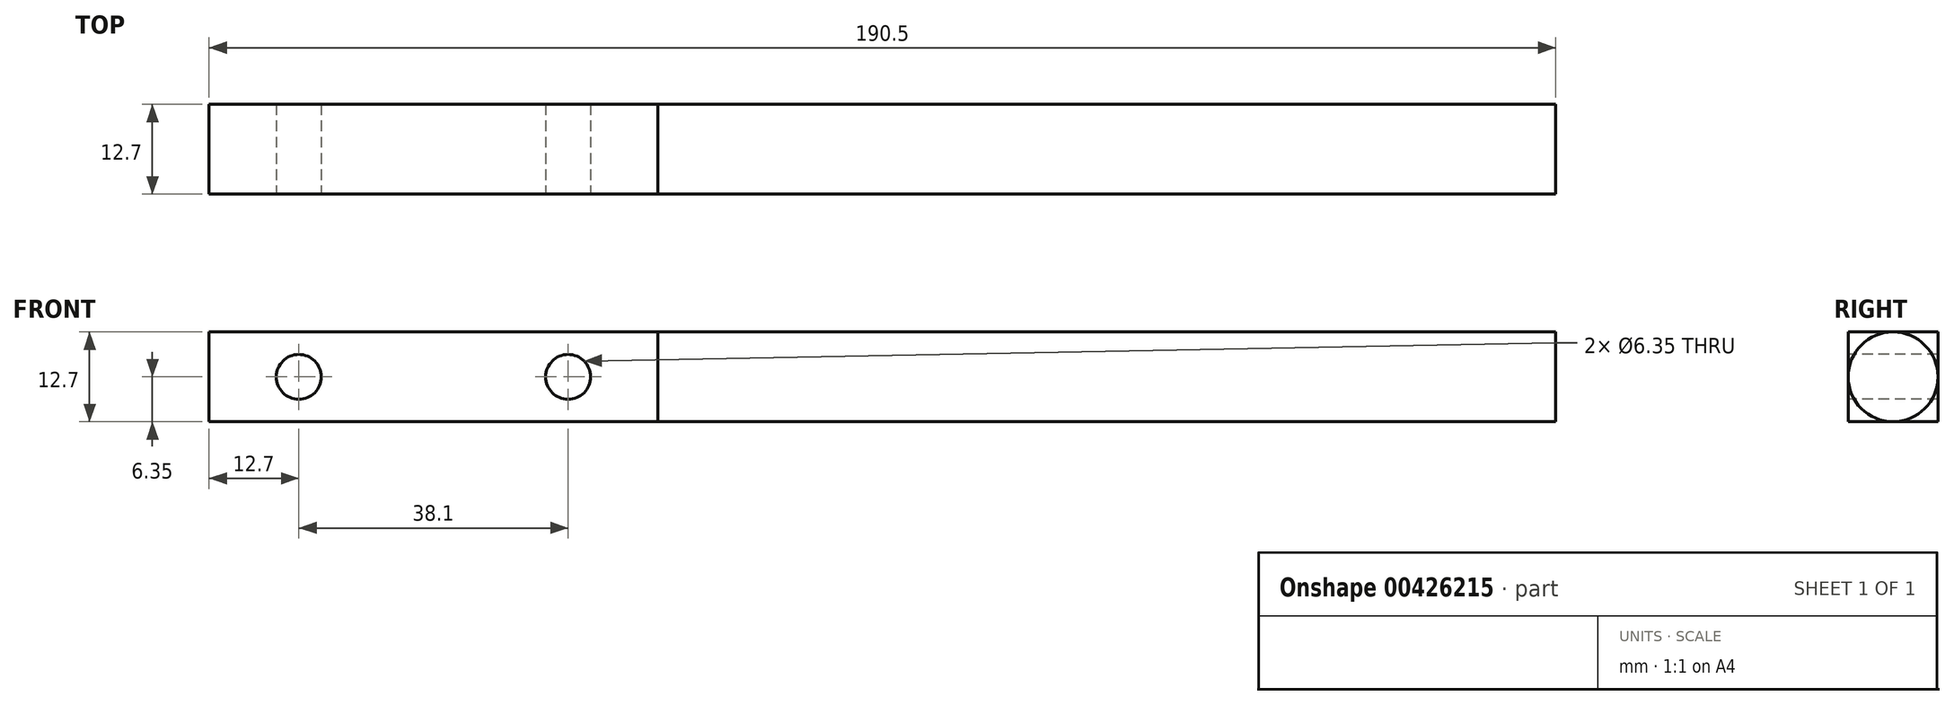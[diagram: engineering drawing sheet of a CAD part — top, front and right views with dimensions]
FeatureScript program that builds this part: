
annotation { "Feature Type Name" : "Feature", "Feature Type Description" : "" }
export const myFeature = defineFeature(function(context is Context, id is Id, definition is map)
    precondition{}
    {
        {
            var Q0;
            Q0=qCreatedBy(makeId("Right.planeOp"),FACE);
            var sketch = newSketch(context, id + "F0", { "sketchPlane" : qUnion([Q0])});
            skLineSegment(sketch, "E0.bottom", {"start": v(0, 0) * mm, "end": v(12.7, 0) * mm});
            skLineSegment(sketch, "E0.top", {"start": v(0, 12.7) * mm, "end": v(12.7, 12.7) * mm});
            skLineSegment(sketch, "E0.left", {"start": v(0, 0) * mm, "end": v(0, 12.7) * mm});
            skLineSegment(sketch, "E0.right", {"start": v(12.7, 0) * mm, "end": v(12.7, 12.7) * mm});
            skSolve(sketch);
        }
        {
            var Q0;
            Q0 = qSketchRegion(id + "F0", true);
            extrude(context, id + "F1", {"entities" : qUnion([Q0]), "depth" : 63.5 * mm});
        }
        {
            var Q0;
            Q0=makeQuery(id+"F1.opExtrude","CAP_FACE",FACE,{"disambiguationData":[OSD([sQuery(id+"F0.wireOp",EDGE,"E0.bottom"),sQuery(id+"F0.wireOp",EDGE,"E0.top"),sQuery(id+"F0.wireOp",EDGE,"E0.left"),sQuery(id+"F0.wireOp",EDGE,"E0.right")])],"isStart":false});
            var sketch = newSketch(context, id + "F2", { "sketchPlane" : qUnion([Q0])});
            skCircle(sketch, "E1", {"center": v(6.35, 6.35) * mm, "radius": 6.35 * mm});
            skSolve(sketch);
        }
        {
            var Q0;
            Q0 = qSketchRegion(id + "F2", true);
            extrude(context, id + "F3", {"entities" : qUnion([Q0]), "operationType" : NewBodyOperationType.ADD, "depth" : 127 * mm});
        }
        {
            var Q0;
            Q0=makeQuery(id+"F1.opExtrude","SWEPT_FACE",FACE,{"disambiguationData":[OSD([sQuery(id+"F0.wireOp",EDGE,"E0.left")])]});
            var sketch = newSketch(context, id + "F4", { "sketchPlane" : qUnion([Q0])});
            skCircle(sketch, "E2", {"center": v(12.7, 6.35) * mm, "radius": 3.18 * mm});
            skCircle(sketch, "E3", {"center": v(50.8, 6.35) * mm, "radius": 3.18 * mm});
            skSolve(sketch);
        }
        {
            var Q0;
            Q0 = qSketchRegion(id + "F4", true);
            extrude(context, id + "F5", {"entities" : qUnion([Q0]), "operationType" : NewBodyOperationType.REMOVE, "endBound" : BoundingType.THROUGH_ALL, "oppositeDirection" : true, "depth" : 25.4 * mm});
        }
    });
